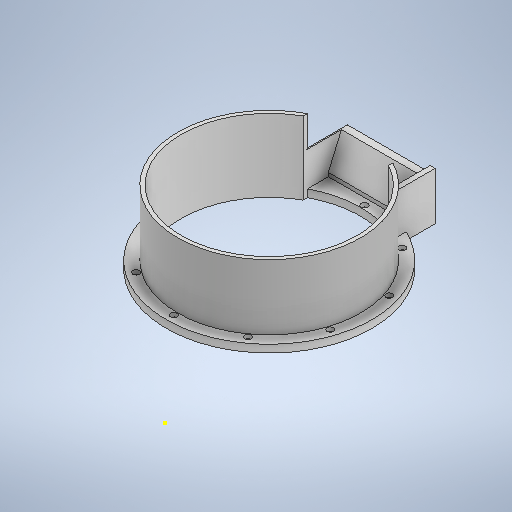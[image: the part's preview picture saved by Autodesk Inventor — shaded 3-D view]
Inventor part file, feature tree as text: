
AUTODESK INVENTOR PART (.ipt)
format: ipt  version: 2025.2 (Build 292293000, 293)  size: 557,568 bytes
history: native  units: in
note: dims shown in document units (in); Inventor stores cm internally (conversion verified against a paired STEP export)
features: extrude x17, sketch x16, other x3, plane x3, chamfer x1, fillet x1
ambient origin geometry x8: Origin, YZ Plane, XZ Plane, XY Plane, X Axis, Y Axis, Z Axis, Center Point
bodies: Body1 (feature_tree)
feature tree (41):
  other  "Cylinder.ipt"
  extrude  "Extrusion1"  Depth=0.3937in
  extrude  "Extrusion2"  Depth=0.3937in TaperAngle=0.0deg
  sketch  "Sketch3"  dims[d7=11.2205in d8=10.6299in]
  extrude  "Extrusion3"  Depth=10.6299in
  extrude  "Extrusion5"  Depth=0.1969in TaperAngle=0.0deg
  sketch  "Sketch6"  dims[d24=0.1969in d25=0.0in d31=0.0in d32=0.0in]
  extrude  "Extrusion6"  Depth=10.6299in
  extrude  "Extrusion7"  TaperAngle=0.0deg  [1 undecoded]
  extrude  "Extrusion8"  Depth=2.1654in
  plane  "Work Plane1"
  extrude  "Extrusion9"  Depth=10.6299in
  extrude  "Extrusion21"  Depth=0.3937in
  sketch  "Sketch19"  dims[d107=2.2047in d108=0.0in d113=2.5591in]
  extrude  "Extrusion34"  Depth=2.5591in
  extrude  "Extrusion43"  Depth=0.0591in
  extrude  "Extrusion53"  Depth=0.0787in
  extrude  "Extrusion44"  Depth=0.0787in
  extrude  "Extrusion45"  TaperAngle=90.0deg  [1 undecoded]
  chamfer  "Chamfer8"  Distance=1.1614in
  plane  "Work Plane2"
  plane  "Work Plane3"
  extrude  "Extrusion55"  Depth=0.2165in
  fillet  "Fillet22"  Radius=0.3425in
  extrude  "Extrusion67"  Depth=0.1969in
  extrude  "Extrusion68"  Depth=0.1969in
  sketch  "Sketch54"  dims[d211=3.937in d213=360.0deg d217=10.4151in d218=9.065in d223=0.5433in d224=1.8228in d225=3.5433in d226=2.564in d227=2.7608in d228=3.5433in d233=7.3568in d234=1.5846in d235=0.0in d236=0.0in d237=1.7717in d238=0.3937in d239=0.0in d240=0.0in d241=0.9843in d242=2.1654in d243=0.0in d244=1.5748in d245=0.0787in d246=0.1598in d263=0.1666in d269=-3.5433in d306=4.5276in d307=0.0591in d308=2.7608in d309=3.5433in d313=3.3661in d314=0.3937in d315=0.0in d316=0.0in d323=0.3937in d324=0.0in d352=0.1969in d372=0.315in d373=0.2559in d374=0.0in d375=0.0591in d376=0.0591in d377=0.1969in d378=0.0in d143=0.0197in d144=0.0344in d145=0.0197in d146=0.0344in d153=0.0in d154=0.0in d155=0.0in d156=0.0in d201=0.0197in d202=0.0344in d203=0.0197in d204=0.0344in d215=0.0197in d216=0.0344in d294=0.0197in d295=0.0344in d296=0.0197in d297=0.0344in d330=0.0197in d331=0.0344in d332=0.0197in d333=0.0344in]
  other  "Solid12::Cylinder.ipt"
  other  "TaggingFeature1"
  sketch  "Sketch1"  dims[d0=0.3937in d2=10.2362in]
  sketch  "Sketch2"  dims[d3=0.0in d4=0.0in d5=0.3937in d6=0.0in]
  sketch  "Sketch5"  dims[d17=10.6299in d18=0.2953in]
  sketch  "Sketch7"  dims[d33=2.1654in d34=0.0in d35=9.8425in]
  sketch  "Sketch9"  dims[d36=10.6299in d46=9.065in]
  sketch  "Sketch14"  dims[d47=0.3937in d48=0.0in d88=0.0787in]
  sketch  "Sketch22"  dims[d117=0.0591in d120=0.5433in]
  sketch  "Sketch Circular Pattern3"  dims[d10=0.1969in d11=0.0in d15=0.1969in d16=0.0in]
  sketch  "Sketch30"  dims[d122=9.4488in d134=0.0787in]
  sketch  "Sketch38"  dims[d164=1.5298in d165=0.0787in]
  sketch  "Sketch52"  dims[d166=1.8325in d167=90.0deg d173=1.1614in d174=0.0in]
  sketch  "Sketch53"  dims[d175=0.0787in d209=0.2165in d210=0.3425in]
note: 2 required parameter values undecoded (feature->parameter linkage not recoverable at this tier; creation-order binding heuristic only, values carry confidence <= 0.55)
